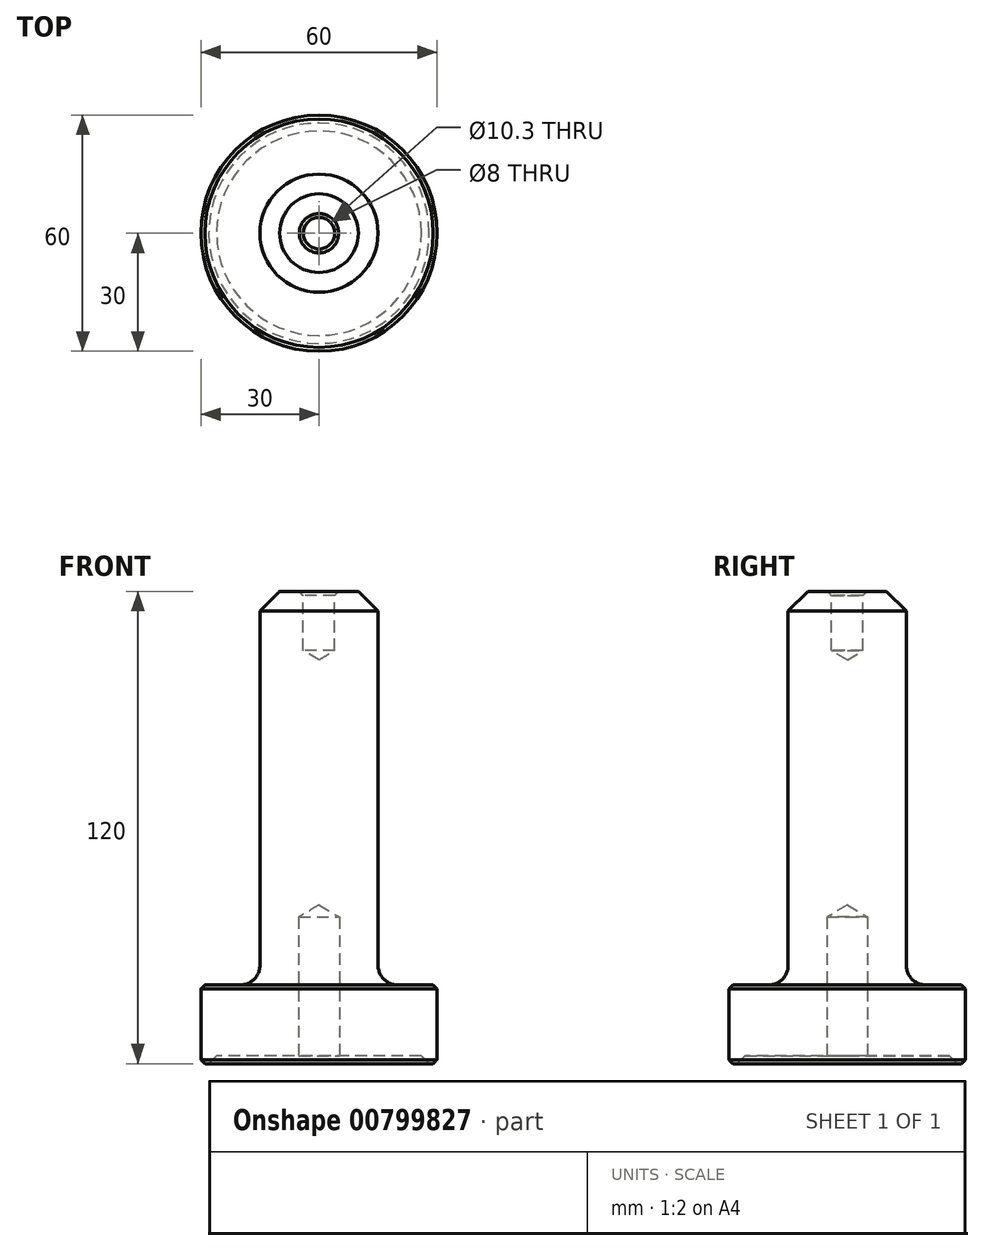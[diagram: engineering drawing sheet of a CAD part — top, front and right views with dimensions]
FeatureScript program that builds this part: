
annotation { "Feature Type Name" : "Feature", "Feature Type Description" : "" }
export const myFeature = defineFeature(function(context is Context, id is Id, definition is map)
    precondition{}
    {
        {
            var Q0;
            Q0=qCreatedBy(makeId("Front.planeOp"),FACE);
            var sketch = newSketch(context, id + "F0", { "sketchPlane" : qUnion([Q0])});
            skLineSegment(sketch, "E0", {"start": v(0, 0) * mm, "end": v(-27, 0) * mm});
            skLineSegment(sketch, "E1", {"start": v(-27, 0) * mm, "end": v(-27, -2) * mm});
            skLineSegment(sketch, "E2", {"start": v(-27, -2) * mm, "end": v(-30, -2) * mm});
            skLineSegment(sketch, "E3", {"start": v(-30, -2) * mm, "end": v(-30, 18) * mm});
            skLineSegment(sketch, "E4", {"start": v(-30, 18) * mm, "end": v(-15, 18) * mm});
            skLineSegment(sketch, "E5", {"start": v(-15, 18) * mm, "end": v(-15, 118) * mm});
            skLineSegment(sketch, "E6", {"start": v(-15, 118) * mm, "end": v(0, 118) * mm});
            skLineSegment(sketch, "E7", {"start": v(0, 118) * mm, "end": v(0, 0) * mm});
            skSolve(sketch);
        }
        {
            var Q0;
            Q0 = qSketchRegion(id + "F0", true);
            var Q1;
            Q1=sQuery(id+"F0.wireOp",EDGE,"E7");
            revolve(context, id + "F1", {"surfaceOperationType" : NewSurfaceOperationType.NEW, "entities" : qUnion([Q0]), "axis" : qUnion([Q1]), "revolveType" : RevolveType.FULL});
        }
        {
            var Q0;
            Q0=makeQuery(id+"F1.opRevolve","SWEPT_EDGE",EDGE,{"disambiguationData":[OSD([sQuery(id+"F0.wireOp",EDGE,"E5"),sQuery(id+"F0.wireOp",EDGE,"E6")])]});
            chamfer(context, id + "F2", {"entities" : qUnion([Q0]), "width" : 5 * mm, "tangentPropagation" : true});
        }
        {
            var Q0;
            Q0=makeQuery(id+"F1.opRevolve","SWEPT_EDGE",EDGE,{"disambiguationData":[OSD([sQuery(id+"F0.wireOp",EDGE,"E3"),sQuery(id+"F0.wireOp",EDGE,"E4")])]});
            var Q1;
            Q1=makeQuery(id+"F1.opRevolve","SWEPT_EDGE",EDGE,{"disambiguationData":[OSD([sQuery(id+"F0.wireOp",EDGE,"E2"),sQuery(id+"F0.wireOp",EDGE,"E3")])]});
            var Q2;
            Q2=makeQuery(id+"F1.opRevolve","SWEPT_FACE",FACE,{"disambiguationData":[OSD([sQuery(id+"F0.wireOp",EDGE,"E1")])]});
            chamfer(context, id + "F3", {"entities" : qUnion([Q0, Q1, Q2]), "width" : 1 * mm, "tangentPropagation" : true});
        }
        {
            var Q0;
            Q0=makeQuery(id+"F1.opRevolve","SWEPT_FACE",FACE,{"disambiguationData":[OSD([sQuery(id+"F0.wireOp",EDGE,"E0")])]});
            var sketch = newSketch(context, id + "F4", { "sketchPlane" : qUnion([Q0])});
            skPoint(sketch, "E8", {"position": v(0, 0) * mm});
            skSolve(sketch);
        }
        {
            var Q0;
            Q0=makeQuery(id+"F1.opRevolve","SWEPT_EDGE",EDGE,{"disambiguationData":[OSD([sQuery(id+"F0.wireOp",EDGE,"E4"),sQuery(id+"F0.wireOp",EDGE,"E5")])]});
            fillet(context, id + "F5", {"entities" : qUnion([Q0]), "radius" : 5 * mm, "tangentPropagation" : true, "allowEdgeOverflow" : false});
        }
        {
            var Q0;
            Q0=sQuery(id+"F4.wireOp",VERTEX,"E8");
            var Q1;
            Q1=makeQuery(id+"F1.opRevolve","SWEPT_BODY",BODY,{"disambiguationData":[OSD([sQuery(id+"F0.wireOp",EDGE,"E0"),sQuery(id+"F0.wireOp",EDGE,"E1"),sQuery(id+"F0.wireOp",EDGE,"E2"),sQuery(id+"F0.wireOp",EDGE,"E3"),sQuery(id+"F0.wireOp",EDGE,"E4"),sQuery(id+"F0.wireOp",EDGE,"E5"),sQuery(id+"F0.wireOp",EDGE,"E6"),sQuery(id+"F0.wireOp",EDGE,"E7")])]});
            hole(context, id + "F6", {"style" : HoleStyle.SIMPLE, "endStyle" : HoleEndStyle.BLIND, "standardTappedOrClearance" : lookupTablePath({ "standard" : "ISO", "engagement" : "75%", "pitch" : "1.75 mm", "size" : "M12", "type" : "Tapped" }), "standardBlindInLast" : lookupTablePath({ "standard" : "ISO", "engagement" : "75%", "pitch" : "1.75 mm", "size" : "M12", "type" : "Tapped" }), "holeDiameter" : 10.3 * mm, "majorDiameter" : 12 * mm, "showTappedDepth" : true, "holeDepth" : 35.25 * mm, "tappedDepth" : 30 * mm, "tapClearance" : 3, "locations" : qUnion([Q0]), "scope" : qUnion([Q1])});
        }
        {
            var Q0;
            Q0=makeQuery(id+"F1.opRevolve","SWEPT_FACE",FACE,{"disambiguationData":[OSD([sQuery(id+"F0.wireOp",EDGE,"E6")])]});
            var sketch = newSketch(context, id + "F7", { "sketchPlane" : qUnion([Q0])});
            skPoint(sketch, "E9", {"position": v(0, 0) * mm});
            skSolve(sketch);
        }
        {
            var Q0;
            Q0=sQuery(id+"F7.wireOp",VERTEX,"E9");
            var Q1;
            Q1=makeQuery(id+"F1.opRevolve","SWEPT_BODY",BODY,{"disambiguationData":[OSD([sQuery(id+"F0.wireOp",EDGE,"E0"),sQuery(id+"F0.wireOp",EDGE,"E1"),sQuery(id+"F0.wireOp",EDGE,"E2"),sQuery(id+"F0.wireOp",EDGE,"E3"),sQuery(id+"F0.wireOp",EDGE,"E4"),sQuery(id+"F0.wireOp",EDGE,"E5"),sQuery(id+"F0.wireOp",EDGE,"E6"),sQuery(id+"F0.wireOp",EDGE,"E7")])]});
            hole(context, id + "F8", {"style" : HoleStyle.C_SINK, "endStyle" : HoleEndStyle.BLIND, "holeDiameter" : 8 * mm, "cSinkDiameter" : 10 * mm, "cSinkAngle" : 90 * degree, "majorDiameter" : 5 * mm, "holeDepth" : 15 * mm, "tappedDepth" : 30 * mm, "tapClearance" : 3, "locations" : qUnion([Q0]), "scope" : qUnion([Q1])});
        }
    });
